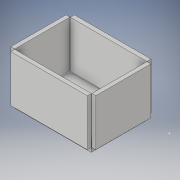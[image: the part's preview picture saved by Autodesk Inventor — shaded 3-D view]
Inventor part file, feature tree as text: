
AUTODESK INVENTOR PART (.ipt)
format: ipt  version: 2019 (Build 230136000, 136)  size: 180,224 bytes
history: native  units: mm
features: sketch x12, extrude x11
ambient origin geometry x8: Origin, YZ Plane, XZ Plane, XY Plane, X Axis, Y Axis, Z Axis, Center Point
bodies: Solid1 (feature_tree)
feature tree (23):
  extrude  "Extrusion1"  Depth=150.0mm
  extrude  "Extrusion2"  Depth=110.0mm TaperAngle=0.0deg
  extrude  "Extrusion3"  Depth=10.0mm TaperAngle=0.0deg
  extrude  "Extrusion4"  Depth=10.0mm TaperAngle=0.0deg
  extrude  "Extrusion5"  Depth=10.0mm TaperAngle=0.0deg
  extrude  "Extrusion6"  Depth=10.0mm TaperAngle=0.0deg
  sketch  "Sketch7"  dims[d22=180.0mm d23=0.0mm]
  extrude  "Extrusion7"  [1 undecoded]
  extrude  "Extrusion8"  [1 undecoded]
  extrude  "Extrusion9"  [1 undecoded]
  extrude  "Extrusion10"  [1 undecoded]
  extrude  "Extrusion11"  [1 undecoded]
  sketch  "Sketch1"  dims[d0=200.0mm d1=150.0mm]
  sketch  "Sketch2"  dims[d2=120.0mm d3=0.0mm d4=110.0mm d5=0.0mm]
  sketch  "Sketch3"  dims[d6=10.0mm d7=0.0mm d8=10.0mm d9=0.0mm]
  sketch  "Sketch4"  dims[d10=10.0mm d11=0.0mm d12=10.0mm d13=0.0mm]
  sketch  "Sketch5"  dims[d14=10.0mm d15=0.0mm d16=10.0mm d17=0.0mm]
  sketch  "Sketch6"  dims[d18=10.0mm d19=0.0mm d20=10.0mm d21=0.0mm]
  sketch  "Sketch8"
  sketch  "Sketch9"
  sketch  "Sketch10"
  sketch  "Sketch11"
  sketch  "Sketch12"
note: 5 required parameter values undecoded (feature->parameter linkage not recoverable at this tier; creation-order binding heuristic only, values carry confidence <= 0.55)
